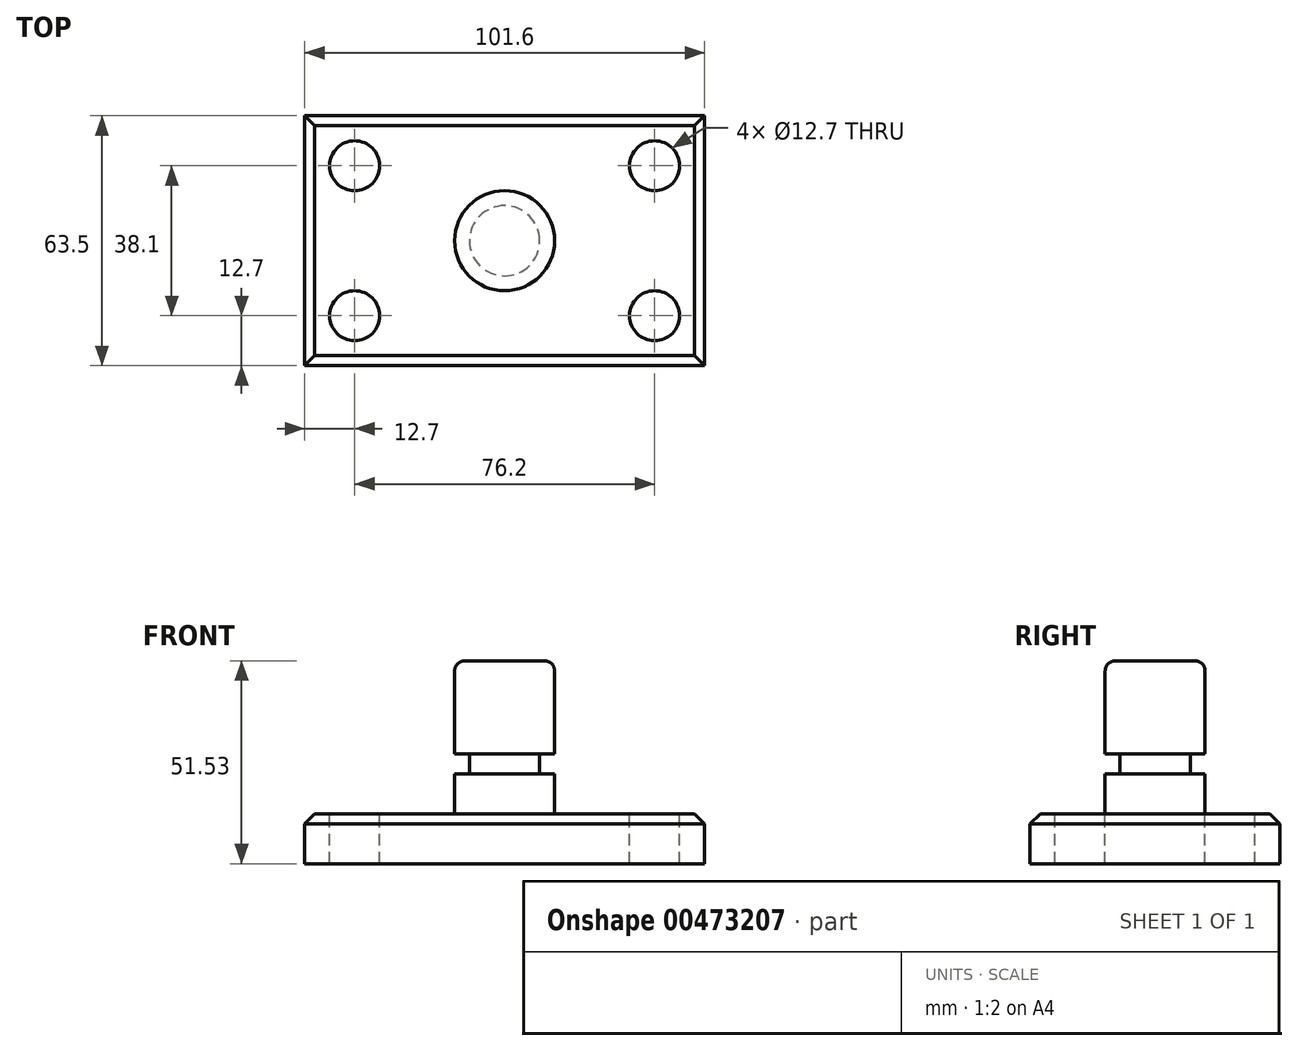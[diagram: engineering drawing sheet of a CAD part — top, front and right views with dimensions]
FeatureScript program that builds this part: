
annotation { "Feature Type Name" : "Feature", "Feature Type Description" : "" }
export const myFeature = defineFeature(function(context is Context, id is Id, definition is map)
    precondition{}
    {
        {
            var Q0;
            Q0=qCreatedBy(makeId("Top.planeOp"),FACE);
            var sketch = newSketch(context, id + "F0", { "sketchPlane" : qUnion([Q0])});
            skLineSegment(sketch, "E0.bottom", {"start": v(50.8, -31.75) * mm, "end": v(-50.8, -31.75) * mm});
            skLineSegment(sketch, "E0.top", {"start": v(50.8, 31.75) * mm, "end": v(-50.8, 31.75) * mm});
            skLineSegment(sketch, "E0.left", {"start": v(50.8, -31.75) * mm, "end": v(50.8, 31.75) * mm});
            skLineSegment(sketch, "E0.right", {"start": v(-50.8, -31.75) * mm, "end": v(-50.8, 31.75) * mm});
            skPoint(sketch, "E0.middle", {"position": v(0, 0) * mm});
            skSolve(sketch);
        }
        {
            var Q0;
            Q0=makeQuery(id+"F0.imprint","IMPRINT",FACE,{"disambiguationData":[TD([[makeQuery(id+"F0.imprint","IMPRINT",EDGE,{"derivedFrom":sQuery(id+"F0.wireOp",EDGE,"E0.bottom")}),-1.0]])]});
            extrude(context, id + "F1", {"entities" : qUnion([Q0]), "depth" : 12.7 * mm});
        }
        {
            var Q0;
            Q0=makeQuery(id+"F1.opExtrude","CAP_FACE",FACE,{"disambiguationData":[OSD([sQuery(id+"F0.wireOp",EDGE,"E0.bottom"),sQuery(id+"F0.wireOp",EDGE,"E0.top"),sQuery(id+"F0.wireOp",EDGE,"E0.left"),sQuery(id+"F0.wireOp",EDGE,"E0.right")])],"isStart":false});
            var sketch = newSketch(context, id + "F2", { "sketchPlane" : qUnion([Q0])});
            skCircle(sketch, "E1", {"center": v(-38.1, 19.05) * mm, "radius": 6.35 * mm});
            skCircle(sketch, "E2", {"center": v(38.1, 19.05) * mm, "radius": 6.35 * mm});
            skCircle(sketch, "E3", {"center": v(38.1, -19.05) * mm, "radius": 6.35 * mm});
            skCircle(sketch, "E4", {"center": v(-38.1, -19.05) * mm, "radius": 6.35 * mm});
            skSolve(sketch);
        }
        {
            var Q0;
            Q0=makeQuery(id+"F2.imprint","IMPRINT",FACE,{"disambiguationData":[TD([[makeQuery(id+"F2.imprint","IMPRINT",EDGE,{"derivedFrom":sQuery(id+"F2.wireOp",EDGE,"E1")}),1.0]])]});
            var Q1;
            Q1=makeQuery(id+"F2.imprint","IMPRINT",FACE,{"disambiguationData":[TD([[makeQuery(id+"F2.imprint","IMPRINT",EDGE,{"derivedFrom":sQuery(id+"F2.wireOp",EDGE,"E4")}),1.0]])]});
            var Q2;
            Q2=makeQuery(id+"F2.imprint","IMPRINT",FACE,{"disambiguationData":[TD([[makeQuery(id+"F2.imprint","IMPRINT",EDGE,{"derivedFrom":sQuery(id+"F2.wireOp",EDGE,"E2")}),1.0]])]});
            var Q3;
            Q3=makeQuery(id+"F2.imprint","IMPRINT",FACE,{"disambiguationData":[TD([[makeQuery(id+"F2.imprint","IMPRINT",EDGE,{"derivedFrom":sQuery(id+"F2.wireOp",EDGE,"E3")}),1.0]])]});
            extrude(context, id + "F3", {"entities" : qUnion([Q0, Q1, Q2, Q3]), "operationType" : NewBodyOperationType.REMOVE, "endBound" : BoundingType.THROUGH_ALL, "oppositeDirection" : true, "depth" : 25.4 * mm});
        }
        {
            var Q0;
            Q0=qCreatedBy(makeId("Front.planeOp"),FACE);
            var sketch = newSketch(context, id + "F4", { "sketchPlane" : qUnion([Q0])});
            skLineSegment(sketch, "E5.bottom", {"start": v(0, 12.7) * mm, "end": v(12.7, 12.7) * mm});
            skLineSegment(sketch, "E5.top", {"start": v(0, 51.53) * mm, "end": v(12.7, 51.53) * mm});
            skLineSegment(sketch, "E5.left", {"start": v(0, 12.7) * mm, "end": v(0, 51.53) * mm});
            skLineSegment(sketch, "E5.right", {"start": v(12.7, 12.7) * mm, "end": v(12.7, 51.53) * mm});
            skSolve(sketch);
        }
        {
            var Q0;
            Q0=makeQuery(id+"F4.imprint","IMPRINT",FACE,{"disambiguationData":[TD([[makeQuery(id+"F4.imprint","IMPRINT",EDGE,{"derivedFrom":sQuery(id+"F4.wireOp",EDGE,"E5.bottom")}),1.0]])]});
            var Q1;
            Q1=sQuery(id+"F4.wireOp",EDGE,"E5.left");
            revolve(context, id + "F5", {"operationType" : NewBodyOperationType.ADD, "entities" : qUnion([Q0]), "axis" : qUnion([Q1]), "revolveType" : RevolveType.FULL});
        }
        {
            var Q0;
            Q0=qCreatedBy(makeId("Front.planeOp"),FACE);
            var sketch = newSketch(context, id + "F6", { "sketchPlane" : qUnion([Q0])});
            skLineSegment(sketch, "E6.bottom", {"start": v(8.92, 27.94) * mm, "end": v(20.91, 27.94) * mm});
            skLineSegment(sketch, "E6.top", {"start": v(8.92, 22.86) * mm, "end": v(20.91, 22.86) * mm});
            skLineSegment(sketch, "E6.left", {"start": v(8.92, 27.94) * mm, "end": v(8.92, 22.86) * mm});
            skLineSegment(sketch, "E6.right", {"start": v(20.91, 27.94) * mm, "end": v(20.91, 22.86) * mm});
            skSolve(sketch);
        }
        {
            var Q0;
            Q0=makeQuery(id+"F6.imprint","IMPRINT",FACE,{"disambiguationData":[TD([[makeQuery(id+"F6.imprint","IMPRINT",EDGE,{"derivedFrom":sQuery(id+"F6.wireOp",EDGE,"E6.bottom")}),-1.0]])]});
            var Q1;
            Q1=makeQuery(id+"F5.opRevolve","SWEPT_FACE",FACE,{"disambiguationData":[OSD([sQuery(id+"F4.wireOp",EDGE,"E5.right")])]});
            revolve(context, id + "F7", {"operationType" : NewBodyOperationType.REMOVE, "entities" : qUnion([Q0]), "axis" : qUnion([Q1]), "revolveType" : RevolveType.FULL, "oppositeDirection" : true});
        }
        {
            var Q0;
            Q0=makeQuery(id+"F5.opRevolve","SWEPT_EDGE",EDGE,{"disambiguationData":[OSD([sQuery(id+"F4.wireOp",EDGE,"E5.bottom"),sQuery(id+"F4.wireOp",EDGE,"E5.right")])]});
            var Q1;
            Q1=makeQuery(id+"F5.opRevolve","SWEPT_EDGE",EDGE,{"disambiguationData":[OSD([sQuery(id+"F4.wireOp",EDGE,"E5.top"),sQuery(id+"F4.wireOp",EDGE,"E5.right")])]});
            fillet(context, id + "F8", {"entities" : qUnion([Q0, Q1]), "radius" : 2.54 * mm, "tangentPropagation" : true, "allowEdgeOverflow" : false});
        }
        {
            var Q0;
            Q0=makeQuery(id+"F1.opExtrude","CAP_EDGE",EDGE,{"disambiguationData":[OSD([sQuery(id+"F0.wireOp",EDGE,"E0.top")])],"isStart":false});
            var Q1;
            Q1=makeQuery(id+"F1.opExtrude","CAP_EDGE",EDGE,{"disambiguationData":[OSD([sQuery(id+"F0.wireOp",EDGE,"E0.right")])],"isStart":false});
            var Q2;
            Q2=makeQuery(id+"F1.opExtrude","CAP_EDGE",EDGE,{"disambiguationData":[OSD([sQuery(id+"F0.wireOp",EDGE,"E0.bottom")])],"isStart":false});
            var Q3;
            Q3=makeQuery(id+"F1.opExtrude","CAP_EDGE",EDGE,{"disambiguationData":[OSD([sQuery(id+"F0.wireOp",EDGE,"E0.left")])],"isStart":false});
            chamfer(context, id + "F9", {"entities" : qUnion([Q0, Q1, Q2, Q3]), "width" : 2.54 * mm, "tangentPropagation" : true});
        }
    });
